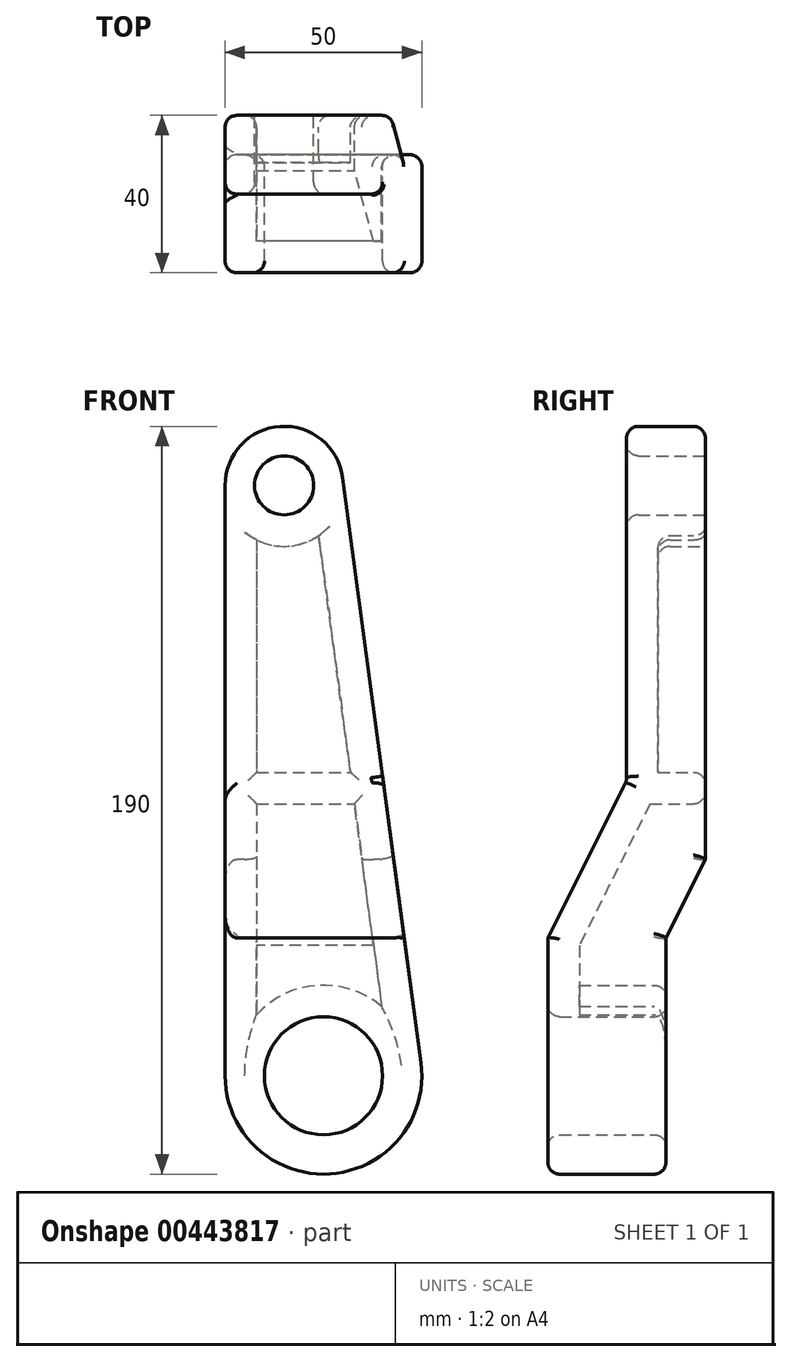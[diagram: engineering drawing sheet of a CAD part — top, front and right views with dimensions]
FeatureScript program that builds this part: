
annotation { "Feature Type Name" : "Feature", "Feature Type Description" : "" }
export const myFeature = defineFeature(function(context is Context, id is Id, definition is map)
    precondition{}
    {
        {
            var Q0;
            Q0=qCreatedBy(makeId("Front.planeOp"),FACE);
            var sketch = newSketch(context, id + "F0", { "sketchPlane" : qUnion([Q0])});
            skArc(sketch, "E0", {"start": v(-25, 0) * mm, "mid": v(1.66, -24.94) * mm, "end": v(24.78, 3.32) * mm});
            skArc(sketch, "E1", {"start": v(4.87, 152) * mm, "mid": v(-11, 164.97) * mm, "end": v(-25, 150) * mm});
            skLineSegment(sketch, "E2", {"start": v(-25, 150) * mm, "end": v(-25, 0) * mm});
            skLineSegment(sketch, "E3", {"start": v(4.87, 152) * mm, "end": v(24.78, 3.32) * mm});
            skSolve(sketch);
        }
        {
            var Q0;
            Q0 = qSketchRegion(id + "F0", true);
            extrude(context, id + "F1", {"entities" : qUnion([Q0]), "depth" : 40 * mm});
        }
        {
            var Q0;
            Q0=makeQuery(id+"F1.opExtrude","SWEPT_FACE",FACE,{"disambiguationData":[OSD([sQuery(id+"F0.wireOp",EDGE,"E2")])]});
            var sketch = newSketch(context, id + "F2", { "sketchPlane" : qUnion([Q0])});
            skLineSegment(sketch, "E4", {"start": v(0, 55) * mm, "end": v(10, 35) * mm});
            skLineSegment(sketch, "E5", {"start": v(0, 55) * mm, "end": v(0, -25.94) * mm});
            skLineSegment(sketch, "E6", {"start": v(10, -25.94) * mm, "end": v(10, 35) * mm});
            skLineSegment(sketch, "E7", {"start": v(40, 35) * mm, "end": v(40, 165.97) * mm});
            skLineSegment(sketch, "E8", {"start": v(20, 165.97) * mm, "end": v(20, 75) * mm});
            skLineSegment(sketch, "E9", {"start": v(20, 75) * mm, "end": v(40, 35) * mm});
            skLineSegment(sketch, "E10", {"start": v(0, -25.94) * mm, "end": v(10, -25.94) * mm});
            skLineSegment(sketch, "E11", {"start": v(20, 165.97) * mm, "end": v(40, 165.97) * mm});
            skSolve(sketch);
        }
        {
            var Q0;
            Q0 = qSketchRegion(id + "F2", true);
            extrude(context, id + "F3", {"entities" : qUnion([Q0]), "operationType" : NewBodyOperationType.REMOVE, "endBound" : BoundingType.THROUGH_ALL, "oppositeDirection" : true, "depth" : 25 * mm});
        }
        {
            var Q0;
            Q0=makeQuery(id+"F1.opExtrude","CAP_FACE",FACE,{"disambiguationData":[OSD([sQuery(id+"F0.wireOp",EDGE,"E0"),sQuery(id+"F0.wireOp",EDGE,"E1"),sQuery(id+"F0.wireOp",EDGE,"E2"),sQuery(id+"F0.wireOp",EDGE,"E3")])],"isStart":true});
            var sketch = newSketch(context, id + "F4", { "sketchPlane" : qUnion([Q0])});
            skCircle(sketch, "E12", {"center": v(10, 150) * mm, "radius": 7.5 * mm});
            skCircle(sketch, "E13", {"center": v(0, 0) * mm, "radius": 15 * mm});
            skSolve(sketch);
        }
        {
            var Q0;
            Q0 = qSketchRegion(id + "F4", true);
            extrude(context, id + "F5", {"entities" : qUnion([Q0]), "operationType" : NewBodyOperationType.REMOVE, "endBound" : BoundingType.THROUGH_ALL, "oppositeDirection" : true, "depth" : 25 * mm});
        }
        {
            var Q0;
            Q0=makeQuery(id+"F1.opExtrude","CAP_FACE",FACE,{"disambiguationData":[OSD([sQuery(id+"F0.wireOp",EDGE,"E0"),sQuery(id+"F0.wireOp",EDGE,"E1"),sQuery(id+"F0.wireOp",EDGE,"E2"),sQuery(id+"F0.wireOp",EDGE,"E3")])],"isStart":true});
            var Q1;
            Q1=makeQuery(id+"F3.boolean.opBoolean","COPY",FACE,{"derivedFrom":makeQuery(id+"F3.opExtrude","SWEPT_FACE",FACE,{"disambiguationData":[OSD([sQuery(id+"F2.wireOp",EDGE,"E4")])]})});
            var Q2;
            Q2=makeQuery(id+"F3.boolean.opBoolean","COPY",FACE,{"derivedFrom":makeQuery(id+"F3.opExtrude","SWEPT_FACE",FACE,{"disambiguationData":[OSD([sQuery(id+"F2.wireOp",EDGE,"E6")])]})});
            shell(context, id + "F6", {"entities" : qUnion([Q0, Q1, Q2]), "thickness" : 8 * mm});
        }
        {
            var Q0;
            Q0=makeQuery(id+"F1.opExtrude","CAP_FACE",FACE,{"disambiguationData":[OSD([sQuery(id+"F0.wireOp",EDGE,"E0"),sQuery(id+"F0.wireOp",EDGE,"E1"),sQuery(id+"F0.wireOp",EDGE,"E2"),sQuery(id+"F0.wireOp",EDGE,"E3")])],"isStart":true});
            var sketch = newSketch(context, id + "F7", { "sketchPlane" : qUnion([Q0])});
            skLineSegment(sketch, "E14", {"start": v(-6.82, 77.11) * mm, "end": v(17, 77.11) * mm});
            skLineSegment(sketch, "E15", {"start": v(-7.9, 69.11) * mm, "end": v(17, 69.11) * mm});
            skLineSegment(sketch, "E16.0", {"start": v(-6.82, 77.11) * mm, "end": v(-7.9, 69.11) * mm});
            skLineSegment(sketch, "E17.0", {"start": v(17, 77.11) * mm, "end": v(17, 69.11) * mm});
            skPoint(sketch, "E18.orphan", {"position": v(-9.79, 55) * mm});
            skPoint(sketch, "E19.orphan", {"position": v(17, 55) * mm});
            skPoint(sketch, "E20.orphan", {"position": v(1.23, 137.22) * mm});
            skPoint(sketch, "E21.orphan", {"position": v(17, 136.17) * mm});
            skSolve(sketch);
        }
        {
            var Q0;
            Q0 = qSketchRegion(id + "F7", true);
            extrude(context, id + "F8", {"entities" : qUnion([Q0]), "operationType" : NewBodyOperationType.ADD, "endBound" : BoundingType.UP_TO_NEXT, "oppositeDirection" : true, "depth" : 25 * mm});
        }
        {
            var Q0;
            Q0=makeQuery(id+"F3.boolean.opBoolean","INTERSECT",EDGE,{"derivedFrom":[makeQuery(id+"F1.opExtrude","SWEPT_FACE",FACE,{"disambiguationData":[OSD([sQuery(id+"F0.wireOp",EDGE,"E3")])]}),makeQuery(id+"F3.opExtrude","SWEPT_FACE",FACE,{"disambiguationData":[OSD([sQuery(id+"F2.wireOp",EDGE,"E8")])]})]});
            var Q1;
            Q1=makeQuery(id+"F3.boolean.opBoolean","INTERSECT",EDGE,{"derivedFrom":[makeQuery(id+"F1.opExtrude","SWEPT_FACE",FACE,{"disambiguationData":[OSD([sQuery(id+"F0.wireOp",EDGE,"E1")])]}),makeQuery(id+"F3.opExtrude","SWEPT_FACE",FACE,{"disambiguationData":[OSD([sQuery(id+"F2.wireOp",EDGE,"E8")])]})]});
            var Q2;
            Q2=makeQuery(id+"F3.boolean.opBoolean","COPY",EDGE,{"derivedFrom":makeQuery(id+"F3.opExtrude","CAP_EDGE",EDGE,{"disambiguationData":[OSD([sQuery(id+"F2.wireOp",EDGE,"E8")])],"isStart":true})});
            var Q3;
            Q3=makeQuery(id+"F3.boolean.opBoolean","COPY",EDGE,{"derivedFrom":makeQuery(id+"F3.opExtrude","CAP_EDGE",EDGE,{"disambiguationData":[OSD([sQuery(id+"F2.wireOp",EDGE,"E9")])],"isStart":true})});
            var Q4;
            Q4=makeQuery(id+"F3.boolean.opBoolean","INTERSECT",EDGE,{"derivedFrom":[makeQuery(id+"F1.opExtrude","SWEPT_FACE",FACE,{"disambiguationData":[OSD([sQuery(id+"F0.wireOp",EDGE,"E3")])]}),makeQuery(id+"F3.opExtrude","SWEPT_FACE",FACE,{"disambiguationData":[OSD([sQuery(id+"F2.wireOp",EDGE,"E9")])]})]});
            var Q5;
            Q5=makeQuery(id+"F1.opExtrude","CAP_EDGE",EDGE,{"disambiguationData":[OSD([sQuery(id+"F0.wireOp",EDGE,"E3")])],"isStart":false});
            var Q6;
            Q6=makeQuery(id+"F1.opExtrude","CAP_EDGE",EDGE,{"disambiguationData":[OSD([sQuery(id+"F0.wireOp",EDGE,"E0")])],"isStart":false});
            var Q7;
            Q7=makeQuery(id+"F1.opExtrude","CAP_EDGE",EDGE,{"disambiguationData":[OSD([sQuery(id+"F0.wireOp",EDGE,"E2")])],"isStart":false});
            var Q8;
            Q8=makeQuery(id+"F3.boolean.opBoolean","INTERSECT",EDGE,{"derivedFrom":[makeQuery(id+"F1.opExtrude","SWEPT_FACE",FACE,{"disambiguationData":[OSD([sQuery(id+"F0.wireOp",EDGE,"E0")])]}),makeQuery(id+"F3.opExtrude","SWEPT_FACE",FACE,{"disambiguationData":[OSD([sQuery(id+"F2.wireOp",EDGE,"E6")])]})]});
            var Q9;
            Q9=makeQuery(id+"F3.boolean.opBoolean","INTERSECT",EDGE,{"derivedFrom":[makeQuery(id+"F1.opExtrude","SWEPT_FACE",FACE,{"disambiguationData":[OSD([sQuery(id+"F0.wireOp",EDGE,"E3")])]}),makeQuery(id+"F3.opExtrude","SWEPT_FACE",FACE,{"disambiguationData":[OSD([sQuery(id+"F2.wireOp",EDGE,"E6")])]})]});
            var Q10;
            Q10=makeQuery(id+"F3.boolean.opBoolean","INTERSECT",EDGE,{"derivedFrom":[makeQuery(id+"F1.opExtrude","SWEPT_FACE",FACE,{"disambiguationData":[OSD([sQuery(id+"F0.wireOp",EDGE,"E3")])]}),makeQuery(id+"F3.opExtrude","SWEPT_FACE",FACE,{"disambiguationData":[OSD([sQuery(id+"F2.wireOp",EDGE,"E4")])]})]});
            var Q11;
            Q11=makeQuery(id+"F1.opExtrude","CAP_EDGE",EDGE,{"disambiguationData":[OSD([sQuery(id+"F0.wireOp",EDGE,"E3")])],"isStart":true});
            var Q12;
            Q12=makeQuery(id+"F1.opExtrude","CAP_EDGE",EDGE,{"disambiguationData":[OSD([sQuery(id+"F0.wireOp",EDGE,"E1")])],"isStart":true});
            var Q13;
            Q13=makeQuery(id+"F1.opExtrude","CAP_EDGE",EDGE,{"disambiguationData":[OSD([sQuery(id+"F0.wireOp",EDGE,"E2")])],"isStart":true});
            var Q14;
            Q14=makeQuery(id+"F3.boolean.opBoolean","COPY",EDGE,{"derivedFrom":makeQuery(id+"F3.opExtrude","CAP_EDGE",EDGE,{"disambiguationData":[OSD([sQuery(id+"F2.wireOp",EDGE,"E4")])],"isStart":true})});
            var Q15;
            Q15=makeQuery(id+"F3.boolean.opBoolean","COPY",EDGE,{"derivedFrom":makeQuery(id+"F3.opExtrude","CAP_EDGE",EDGE,{"disambiguationData":[OSD([sQuery(id+"F2.wireOp",EDGE,"E6")])],"isStart":true})});
            var Q16;
            Q16=makeQuery(id+"F5.boolean.opBoolean","INTERSECT",EDGE,{"derivedFrom":[makeQuery(id+"F1.opExtrude","CAP_FACE",FACE,{"disambiguationData":[OSD([sQuery(id+"F0.wireOp",EDGE,"E0"),sQuery(id+"F0.wireOp",EDGE,"E1"),sQuery(id+"F0.wireOp",EDGE,"E2"),sQuery(id+"F0.wireOp",EDGE,"E3")])],"isStart":false}),makeQuery(id+"F5.opExtrude","SWEPT_FACE",FACE,{"disambiguationData":[OSD([sQuery(id+"F4.wireOp",EDGE,"E13")])]})]});
            var Q17;
            Q17=makeQuery(id+"F5.boolean.opBoolean","INTERSECT",EDGE,{"derivedFrom":[makeQuery(id+"F3.boolean.opBoolean","COPY",FACE,{"derivedFrom":makeQuery(id+"F3.opExtrude","SWEPT_FACE",FACE,{"disambiguationData":[OSD([sQuery(id+"F2.wireOp",EDGE,"E6")])]})}),makeQuery(id+"F5.opExtrude","SWEPT_FACE",FACE,{"disambiguationData":[OSD([sQuery(id+"F4.wireOp",EDGE,"E13")])]})]});
            var Q18;
            {var subQ1=sQuery(id+"F0.wireOp",EDGE,"E3");Q18=makeQuery(id+"F8.boolean.opBoolean","SPLIT",EDGE,{"disambiguationData":[TD([makeQuery(id+"F6.opShell","OFFSET_FACE",FACE,{"disambiguationData":[OSD([sQuery(id+"F4.wireOp",EDGE,"E12")])]})])],"derivedFrom":makeQuery(id+"F6.opShell","OFFSET_EDGE",EDGE,{"disambiguationData":[OSD([subQ1]),TDD([makeQuery(id+"F1.opExtrude","CAP_EDGE",EDGE,{"disambiguationData":[OSD([subQ1])],"isStart":true})])]})});}
            var Q19;
            Q19=makeQuery(id+"F6.opShell","OFFSET_EDGE",EDGE,{"disambiguationData":[OSD([sQuery(id+"F4.wireOp",EDGE,"E12")])]});
            var Q20;
            Q20=makeQuery(id+"F5.boolean.opBoolean","COPY",EDGE,{"derivedFrom":makeQuery(id+"F5.opExtrude","CAP_EDGE",EDGE,{"disambiguationData":[OSD([sQuery(id+"F4.wireOp",EDGE,"E12")])],"isStart":true})});
            var Q21;
            Q21=makeQuery(id+"F8.opExtrude","CAP_EDGE",EDGE,{"disambiguationData":[OSD([sQuery(id+"F7.wireOp",EDGE,"E15")])],"isStart":true});
            var Q22;
            {var subQ1=sQuery(id+"F0.wireOp",EDGE,"E3");Q22=makeQuery(id+"F8.boolean.opBoolean","SPLIT",EDGE,{"disambiguationData":[TD([makeQuery(id+"F3.boolean.opBoolean","COPY",FACE,{"derivedFrom":makeQuery(id+"F3.opExtrude","SWEPT_FACE",FACE,{"disambiguationData":[OSD([sQuery(id+"F2.wireOp",EDGE,"E4")])]})})])],"derivedFrom":makeQuery(id+"F6.opShell","OFFSET_EDGE",EDGE,{"disambiguationData":[OSD([subQ1]),TDD([makeQuery(id+"F1.opExtrude","CAP_EDGE",EDGE,{"disambiguationData":[OSD([subQ1])],"isStart":true})])]})});}
            var Q23;
            Q23=makeQuery(id+"F6.opShell","OFFSET_EDGE",EDGE,{"disambiguationData":[OSD([sQuery(id+"F0.wireOp",EDGE,"E3"),sQuery(id+"F2.wireOp",EDGE,"E4")])]});
            var Q24;
            Q24=makeQuery(id+"F6.opShell","OFFSET_EDGE",EDGE,{"disambiguationData":[OSD([sQuery(id+"F0.wireOp",EDGE,"E3"),sQuery(id+"F2.wireOp",EDGE,"E6")])]});
            var Q25;
            Q25=makeQuery(id+"F6.opShell","OFFSET_EDGE",EDGE,{"disambiguationData":[OSD([sQuery(id+"F2.wireOp",EDGE,"E6"),sQuery(id+"F4.wireOp",EDGE,"E13")])]});
            var Q26;
            Q26=makeQuery(id+"F6.opShell","OFFSET_EDGE",EDGE,{"disambiguationData":[OSD([sQuery(id+"F2.wireOp",EDGE,"E6")])]});
            var Q27;
            Q27=makeQuery(id+"F6.opShell","OFFSET_EDGE",EDGE,{"disambiguationData":[OSD([sQuery(id+"F2.wireOp",EDGE,"E4")])]});
            var Q28;
            {var subQ1=sQuery(id+"F0.wireOp",EDGE,"E2");Q28=makeQuery(id+"F8.boolean.opBoolean","SPLIT",EDGE,{"disambiguationData":[TD([makeQuery(id+"F6.opShell","OFFSET_FACE",FACE,{"disambiguationData":[OSD([sQuery(id+"F2.wireOp",EDGE,"E4")])]})])],"derivedFrom":makeQuery(id+"F6.opShell","OFFSET_EDGE",EDGE,{"disambiguationData":[OSD([subQ1]),TDD([makeQuery(id+"F1.opExtrude","CAP_EDGE",EDGE,{"disambiguationData":[OSD([subQ1])],"isStart":true})])]})});}
            var Q29;
            Q29=makeQuery(id+"F5.boolean.opBoolean","INTERSECT",EDGE,{"derivedFrom":[makeQuery(id+"F3.boolean.opBoolean","COPY",FACE,{"derivedFrom":makeQuery(id+"F3.opExtrude","SWEPT_FACE",FACE,{"disambiguationData":[OSD([sQuery(id+"F2.wireOp",EDGE,"E8")])]})}),makeQuery(id+"F5.opExtrude","SWEPT_FACE",FACE,{"disambiguationData":[OSD([sQuery(id+"F4.wireOp",EDGE,"E12")])]})]});
            var Q30;
            Q30=makeQuery(id+"F8.opExtrude","CAP_EDGE",EDGE,{"disambiguationData":[OSD([sQuery(id+"F7.wireOp",EDGE,"E14")])],"isStart":true});
            var Q31;
            {var subQ1=sQuery(id+"F0.wireOp",EDGE,"E2");Q31=makeQuery(id+"F8.boolean.opBoolean","SPLIT",EDGE,{"disambiguationData":[TD([makeQuery(id+"F6.opShell","OFFSET_FACE",FACE,{"disambiguationData":[OSD([sQuery(id+"F4.wireOp",EDGE,"E12")])]})])],"derivedFrom":makeQuery(id+"F6.opShell","OFFSET_EDGE",EDGE,{"disambiguationData":[OSD([subQ1]),TDD([makeQuery(id+"F1.opExtrude","CAP_EDGE",EDGE,{"disambiguationData":[OSD([subQ1])],"isStart":true})])]})});}
            var Q32;
            Q32=makeQuery(id+"F3.boolean.opBoolean","COPY",EDGE,{"derivedFrom":makeQuery(id+"F3.opExtrude","SWEPT_EDGE",EDGE,{"disambiguationData":[OSD([sQuery(id+"F0.wireOp",EDGE,"E2"),sQuery(id+"F2.wireOp",EDGE,"E7"),sQuery(id+"F2.wireOp",EDGE,"E9")])]})});
            var Q33;
            Q33=makeQuery(id+"F3.boolean.opBoolean","COPY",EDGE,{"derivedFrom":makeQuery(id+"F3.opExtrude","SWEPT_EDGE",EDGE,{"disambiguationData":[OSD([sQuery(id+"F2.wireOp",EDGE,"E8"),sQuery(id+"F2.wireOp",EDGE,"E9")])]})});
            fillet(context, id + "F9", {"entities" : qUnion([Q0, Q1, Q2, Q3, Q4, Q5, Q6, Q7, Q8, Q9, Q10, Q11, Q12, Q13, Q14, Q15, Q16, Q17, Q18, Q19, Q20, Q21, Q22, Q23, Q24, Q25, Q26, Q27, Q28, Q29, Q30, Q31, Q32, Q33]), "radius" : 3 * mm, "tangentPropagation" : true, "allowEdgeOverflow" : false});
        }
    });
